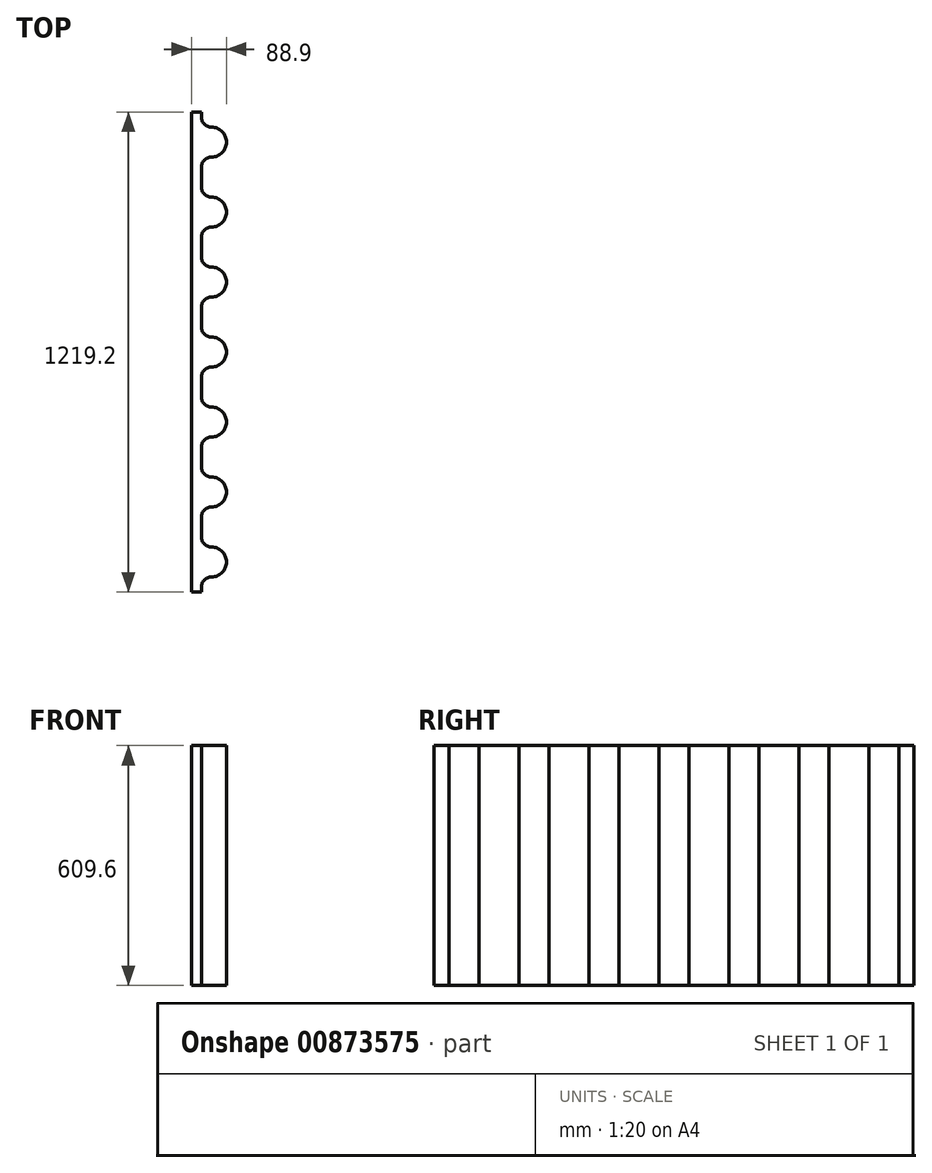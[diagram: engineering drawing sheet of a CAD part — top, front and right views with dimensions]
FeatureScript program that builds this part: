
annotation { "Feature Type Name" : "Feature", "Feature Type Description" : "" }
export const myFeature = defineFeature(function(context is Context, id is Id, definition is map)
    precondition{}
    {
        {
            var Q0;
            Q0=qCreatedBy(makeId("Top.planeOp"),FACE);
            var sketch = newSketch(context, id + "F0", { "sketchPlane" : qUnion([Q0])});
            skLineSegment(sketch, "E0.bottom", {"start": v(0, 0) * mm, "end": v(25.4, 0) * mm});
            skLineSegment(sketch, "E0.top", {"start": v(0, 1219.2) * mm, "end": v(25.4, 1219.2) * mm});
            skLineSegment(sketch, "E0.left", {"start": v(0, 0) * mm, "end": v(0, 1219.2) * mm});
            skLineSegment(sketch, "E0.right", {"start": v(25.4, 0) * mm, "end": v(25.4, 546.1) * mm});
            skLineSegment(sketch, "E1", {"start": v(-81.23, 609.6) * mm, "end": v(258.04, 609.6) * mm, "construction": true});
            skPoint(sketch, "E1.startSnap0", {"position": v(0, 609.6) * mm});
            skLineSegment(sketch, "E2.0", {"start": v(50.8, 0) * mm, "end": v(50.8, 1219.2) * mm, "construction": true});
            skArc(sketch, "E3", {"start": v(50.8, 571.5) * mm, "mid": v(88.9, 609.6) * mm, "end": v(50.8, 647.7) * mm});
            skArc(sketch, "E4", {"start": v(50.8, 647.7) * mm, "mid": v(32.84, 655.14) * mm, "end": v(25.4, 673.1) * mm});
            skArc(sketch, "E5", {"start": v(50.8, 571.5) * mm, "mid": v(32.84, 564.06) * mm, "end": v(25.4, 546.1) * mm});
            skLineSegment(sketch, "E6.trimOffspring", {"start": v(25.4, 673.1) * mm, "end": v(25.4, 1219.2) * mm});
            skArc(sketch, "E7.0.1.0", {"start": v(50.8, 825.5) * mm, "mid": v(32.84, 832.94) * mm, "end": v(25.4, 850.9) * mm});
            skArc(sketch, "E7.0.1.1", {"start": v(50.8, 749.3) * mm, "mid": v(88.9, 787.4) * mm, "end": v(50.8, 825.5) * mm});
            skArc(sketch, "E7.0.1.2", {"start": v(50.8, 749.3) * mm, "mid": v(32.84, 741.86) * mm, "end": v(25.4, 723.9) * mm});
            skArc(sketch, "E7.0.2.0", {"start": v(50.8, 1003.3) * mm, "mid": v(32.84, 1010.74) * mm, "end": v(25.4, 1028.7) * mm});
            skArc(sketch, "E7.0.2.1", {"start": v(50.8, 927.1) * mm, "mid": v(88.9, 965.2) * mm, "end": v(50.8, 1003.3) * mm});
            skArc(sketch, "E7.0.2.2", {"start": v(50.8, 927.1) * mm, "mid": v(32.84, 919.66) * mm, "end": v(25.4, 901.7) * mm});
            skArc(sketch, "E7.0.3.0", {"start": v(50.8, 1181.1) * mm, "mid": v(32.84, 1188.54) * mm, "end": v(25.4, 1206.5) * mm});
            skArc(sketch, "E7.0.3.1", {"start": v(50.8, 1104.9) * mm, "mid": v(88.9, 1143) * mm, "end": v(50.8, 1181.1) * mm});
            skArc(sketch, "E7.0.3.2", {"start": v(50.8, 1104.9) * mm, "mid": v(32.84, 1097.46) * mm, "end": v(25.4, 1079.5) * mm});
            skLineSegment(sketch, "E7.direction1", {"start": v(50.8, 647.7) * mm, "end": v(314.96, 647.7) * mm, "construction": true});
            skLineSegment(sketch, "E7.direction2", {"start": v(50.8, 647.7) * mm, "end": v(50.8, 825.5) * mm, "construction": true});
            skArc(sketch, "E8.0.1.0", {"start": v(50.8, 393.7) * mm, "mid": v(88.9, 431.8) * mm, "end": v(50.8, 469.9) * mm});
            skArc(sketch, "E8.0.1.1", {"start": v(50.8, 393.7) * mm, "mid": v(32.84, 386.26) * mm, "end": v(25.4, 368.3) * mm});
            skArc(sketch, "E8.0.1.2", {"start": v(50.8, 469.9) * mm, "mid": v(32.84, 477.34) * mm, "end": v(25.4, 495.3) * mm});
            skArc(sketch, "E8.0.2.0", {"start": v(50.8, 215.9) * mm, "mid": v(88.9, 254) * mm, "end": v(50.8, 292.1) * mm});
            skArc(sketch, "E8.0.2.1", {"start": v(50.8, 215.9) * mm, "mid": v(32.84, 208.46) * mm, "end": v(25.4, 190.5) * mm});
            skArc(sketch, "E8.0.2.2", {"start": v(50.8, 292.1) * mm, "mid": v(32.84, 299.54) * mm, "end": v(25.4, 317.5) * mm});
            skArc(sketch, "E8.0.3.0", {"start": v(50.8, 38.1) * mm, "mid": v(88.9, 76.2) * mm, "end": v(50.8, 114.3) * mm});
            skArc(sketch, "E8.0.3.1", {"start": v(50.8, 38.1) * mm, "mid": v(32.84, 30.66) * mm, "end": v(25.4, 12.7) * mm});
            skArc(sketch, "E8.0.3.2", {"start": v(50.8, 114.3) * mm, "mid": v(32.84, 121.74) * mm, "end": v(25.4, 139.7) * mm});
            skLineSegment(sketch, "E8.direction1", {"start": v(50.8, 571.5) * mm, "end": v(76.2, 571.5) * mm, "construction": true});
            skLineSegment(sketch, "E8.direction2", {"start": v(50.8, 571.5) * mm, "end": v(50.8, 393.7) * mm, "construction": true});
            skSolve(sketch);
        }
        {
            var Q0;
            Q0 = qSketchRegion(id + "F0", true);
            extrude(context, id + "F1", {"entities" : qUnion([Q0]), "depth" : 609.6 * mm, "offsetDistance" : 25.4 * mm});
        }
    });
